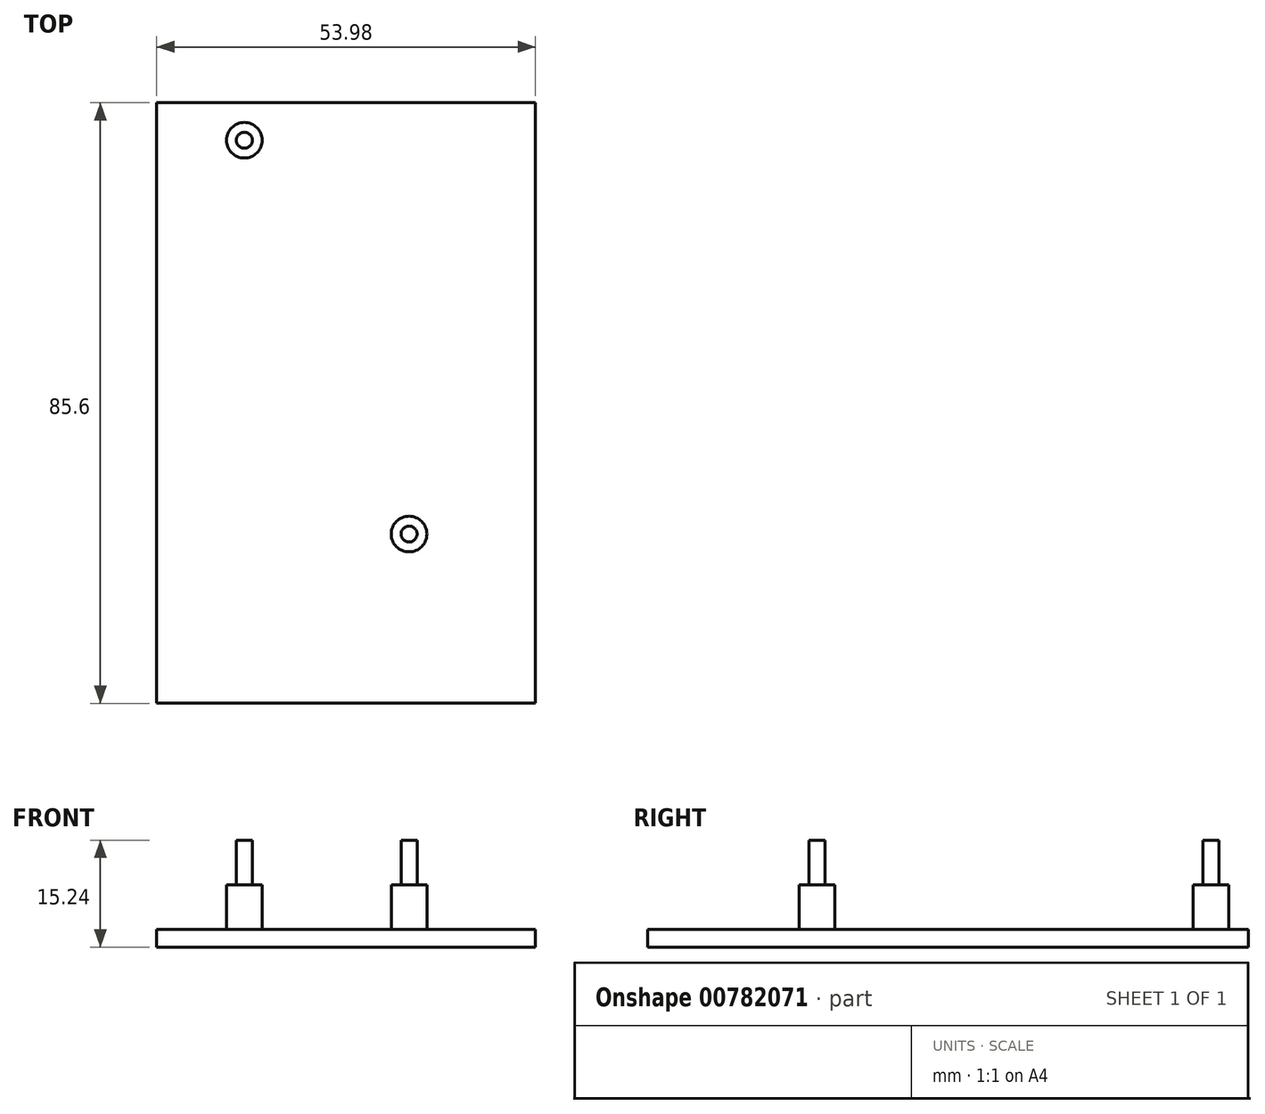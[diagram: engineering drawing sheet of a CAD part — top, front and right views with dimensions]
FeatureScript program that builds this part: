
annotation { "Feature Type Name" : "Feature", "Feature Type Description" : "" }
export const myFeature = defineFeature(function(context is Context, id is Id, definition is map)
    precondition{}
    {
        {
            var Q0;
            Q0=qCreatedBy(makeId("Top.planeOp"),FACE);
            var sketch = newSketch(context, id + "F0", { "sketchPlane" : qUnion([Q0])});
            skLineSegment(sketch, "E0.bottom", {"start": v(0, 0) * mm, "end": v(53.97, 0) * mm});
            skLineSegment(sketch, "E0.top", {"start": v(0, -85.6) * mm, "end": v(53.98, -85.6) * mm});
            skLineSegment(sketch, "E0.left", {"start": v(0, 0) * mm, "end": v(0, -85.6) * mm});
            skLineSegment(sketch, "E0.right", {"start": v(53.97, 0) * mm, "end": v(53.98, -85.6) * mm});
            skSolve(sketch);
        }
        {
            var Q0;
            Q0=makeQuery(id+"F0.imprint","IMPRINT",FACE,{"disambiguationData":[TD([[makeQuery(id+"F0.imprint","IMPRINT",EDGE,{"derivedFrom":sQuery(id+"F0.wireOp",EDGE,"E0.bottom")}),-1.0]])]});
            extrude(context, id + "F1", {"entities" : qUnion([Q0]), "depth" : 2.54 * mm, "offsetDistance" : 25.4 * mm});
        }
        {
            var Q0;
            Q0=makeQuery(id+"F1.opExtrude","CAP_FACE",FACE,{"disambiguationData":[OSD([sQuery(id+"F0.wireOp",EDGE,"E0.bottom"),sQuery(id+"F0.wireOp",EDGE,"E0.top"),sQuery(id+"F0.wireOp",EDGE,"E0.left"),sQuery(id+"F0.wireOp",EDGE,"E0.right")])],"isStart":false});
            var sketch = newSketch(context, id + "F2", { "sketchPlane" : qUnion([Q0])});
            skCircle(sketch, "E1", {"center": v(12.5, -5.33) * mm, "radius": 2.54 * mm});
            skCircle(sketch, "E2", {"center": v(12.5, -5.33) * mm, "radius": 1.14 * mm});
            skLineSegment(sketch, "E3.top", {"start": v(12.5, 0) * mm, "end": v(0, 0) * mm});
            skLineSegment(sketch, "E3.right", {"start": v(0, -5.33) * mm, "end": v(0, 0) * mm});
            skCircle(sketch, "E4", {"center": v(35.97, -61.47) * mm, "radius": 1.14 * mm});
            skCircle(sketch, "E5", {"center": v(35.97, -61.47) * mm, "radius": 2.54 * mm});
            skSolve(sketch);
        }
        {
            var Q0;
            Q0=makeQuery(id+"F2.imprint","IMPRINT",FACE,{"disambiguationData":[TD([[makeQuery(id+"F2.imprint","IMPRINT",EDGE,{"derivedFrom":sQuery(id+"F2.wireOp",EDGE,"E1")}),1.0]])]});
            var Q1;
            Q1=makeQuery(id+"F2.imprint","IMPRINT",FACE,{"disambiguationData":[TD([[makeQuery(id+"F2.imprint","IMPRINT",EDGE,{"derivedFrom":sQuery(id+"F2.wireOp",EDGE,"E4")}),-1.0]])]});
            extrude(context, id + "F3", {"entities" : qUnion([Q0, Q1]), "operationType" : NewBodyOperationType.ADD, "depth" : 6.35 * mm, "offsetDistance" : 25.4 * mm});
        }
        {
            var Q0;
            Q0=makeQuery(id+"F2.imprint","IMPRINT",FACE,{"disambiguationData":[TD([[makeQuery(id+"F2.imprint","IMPRINT",EDGE,{"derivedFrom":sQuery(id+"F2.wireOp",EDGE,"E2")}),1.0]])]});
            var Q1;
            Q1=makeQuery(id+"F2.imprint","IMPRINT",FACE,{"disambiguationData":[TD([[makeQuery(id+"F2.imprint","IMPRINT",EDGE,{"derivedFrom":sQuery(id+"F2.wireOp",EDGE,"E4")}),1.0]])]});
            extrude(context, id + "F4", {"entities" : qUnion([Q0, Q1]), "operationType" : NewBodyOperationType.ADD, "depth" : 12.7 * mm, "offsetDistance" : 25.4 * mm});
        }
    });
